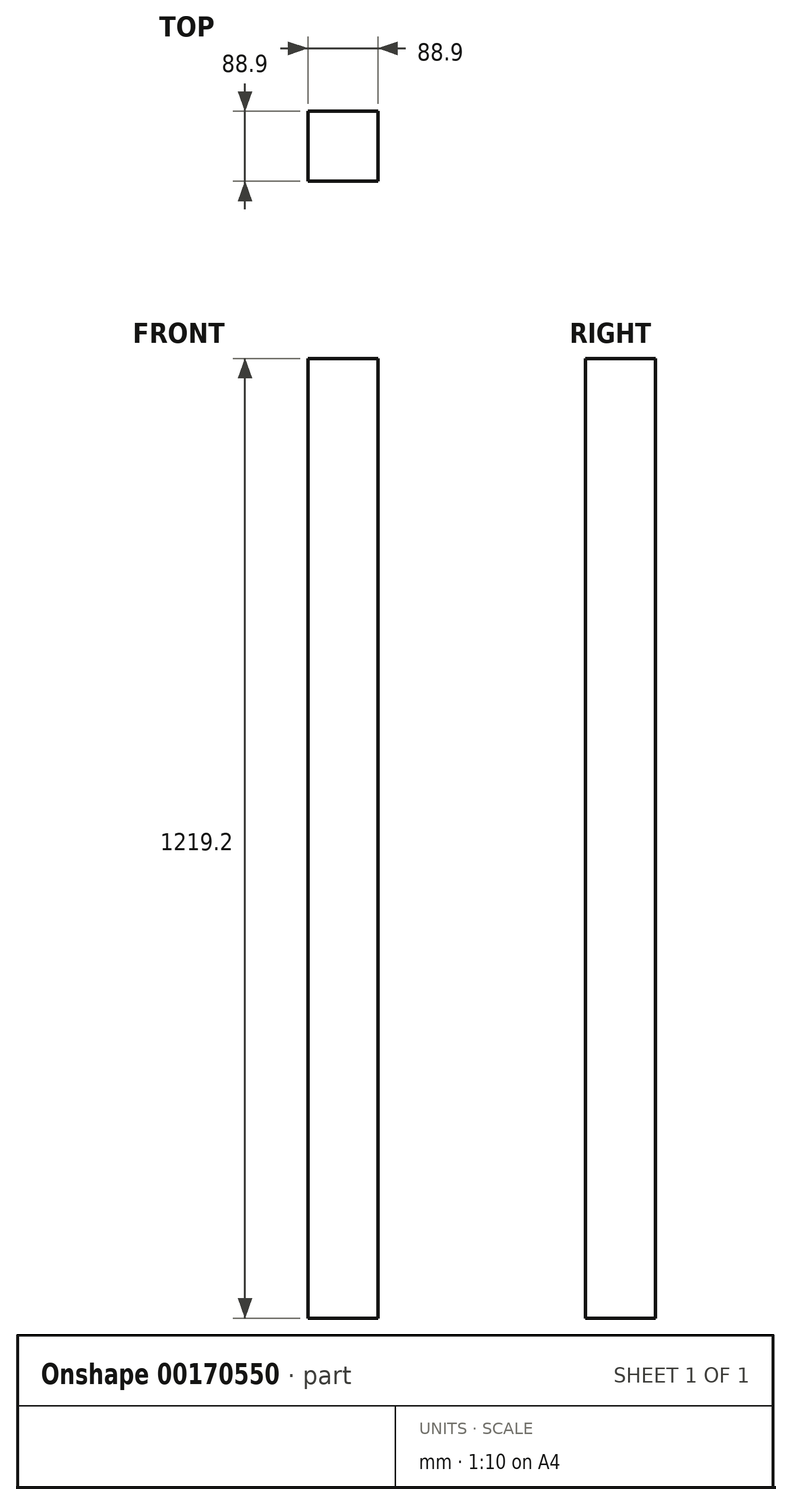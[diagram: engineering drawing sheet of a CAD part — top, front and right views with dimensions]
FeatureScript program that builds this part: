
annotation { "Feature Type Name" : "Feature", "Feature Type Description" : "" }
export const myFeature = defineFeature(function(context is Context, id is Id, definition is map)
    precondition{}
    {
        {
            var Q0;
            Q0=qCreatedBy(makeId("Top.planeOp"),FACE);
            var sketch = newSketch(context, id + "F0", { "sketchPlane" : qUnion([Q0])});
            skLineSegment(sketch, "E0.bottom", {"start": v(0, 0) * mm, "end": v(88.9, 0) * mm});
            skLineSegment(sketch, "E0.top", {"start": v(0, 88.9) * mm, "end": v(88.9, 88.9) * mm});
            skLineSegment(sketch, "E0.left", {"start": v(0, 0) * mm, "end": v(0, 88.9) * mm});
            skLineSegment(sketch, "E0.right", {"start": v(88.9, 0) * mm, "end": v(88.9, 88.9) * mm});
            skSolve(sketch);
        }
        {
            var Q0;
            Q0=makeQuery(id+"F0.imprint","IMPRINT",FACE,{"disambiguationData":[TD([[makeQuery(id+"F0.imprint","IMPRINT",EDGE,{"derivedFrom":sQuery(id+"F0.wireOp",EDGE,"E0.bottom")}),1.0]])]});
            extrude(context, id + "F1", {"entities" : qUnion([Q0]), "depth" : 1219.2 * mm});
        }
    });
